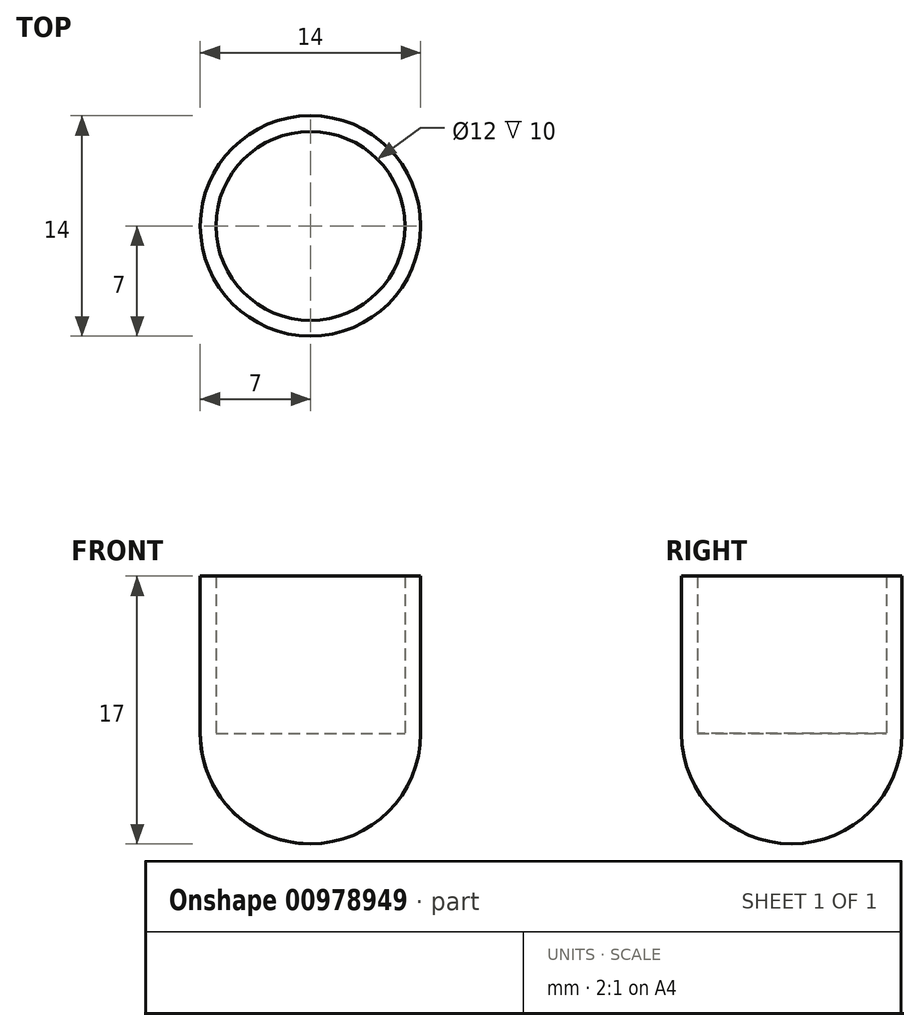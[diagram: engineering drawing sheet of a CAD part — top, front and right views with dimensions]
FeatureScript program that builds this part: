
annotation { "Feature Type Name" : "Feature", "Feature Type Description" : "" }
export const myFeature = defineFeature(function(context is Context, id is Id, definition is map)
    precondition{}
    {
        {
            var Q0;
            Q0=qCreatedBy(makeId("Front.planeOp"),FACE);
            var sketch = newSketch(context, id + "F0", { "sketchPlane" : qUnion([Q0])});
            skArc(sketch, "E0", {"start": v(-7, 0) * mm, "mid": v(-4.95, -4.95) * mm, "end": v(0, -7) * mm});
            skLineSegment(sketch, "E1", {"start": v(-7, 0) * mm, "end": v(-7, 10) * mm});
            skLineSegment(sketch, "E2", {"start": v(-7, 10) * mm, "end": v(-6, 10) * mm});
            skLineSegment(sketch, "E3", {"start": v(-6, 10) * mm, "end": v(-6, 0) * mm});
            skLineSegment(sketch, "E4", {"start": v(-6, 0) * mm, "end": v(0, 0) * mm});
            skLineSegment(sketch, "E5", {"start": v(0, -7) * mm, "end": v(0, 0) * mm});
            skSolve(sketch);
        }
        {
            var Q0;
            Q0=makeQuery(id+"F0.imprint","IMPRINT",FACE,{"disambiguationData":[TD([[makeQuery(id+"F0.imprint","IMPRINT",EDGE,{"derivedFrom":sQuery(id+"F0.wireOp",EDGE,"E0")}),1.0]])]});
            var Q1;
            Q1=sQuery(id+"F0.wireOp",EDGE,"E5");
            revolve(context, id + "F1", {"surfaceOperationType" : NewSurfaceOperationType.NEW, "entities" : qUnion([Q0]), "axis" : qUnion([Q1]), "revolveType" : RevolveType.FULL});
        }
    });
